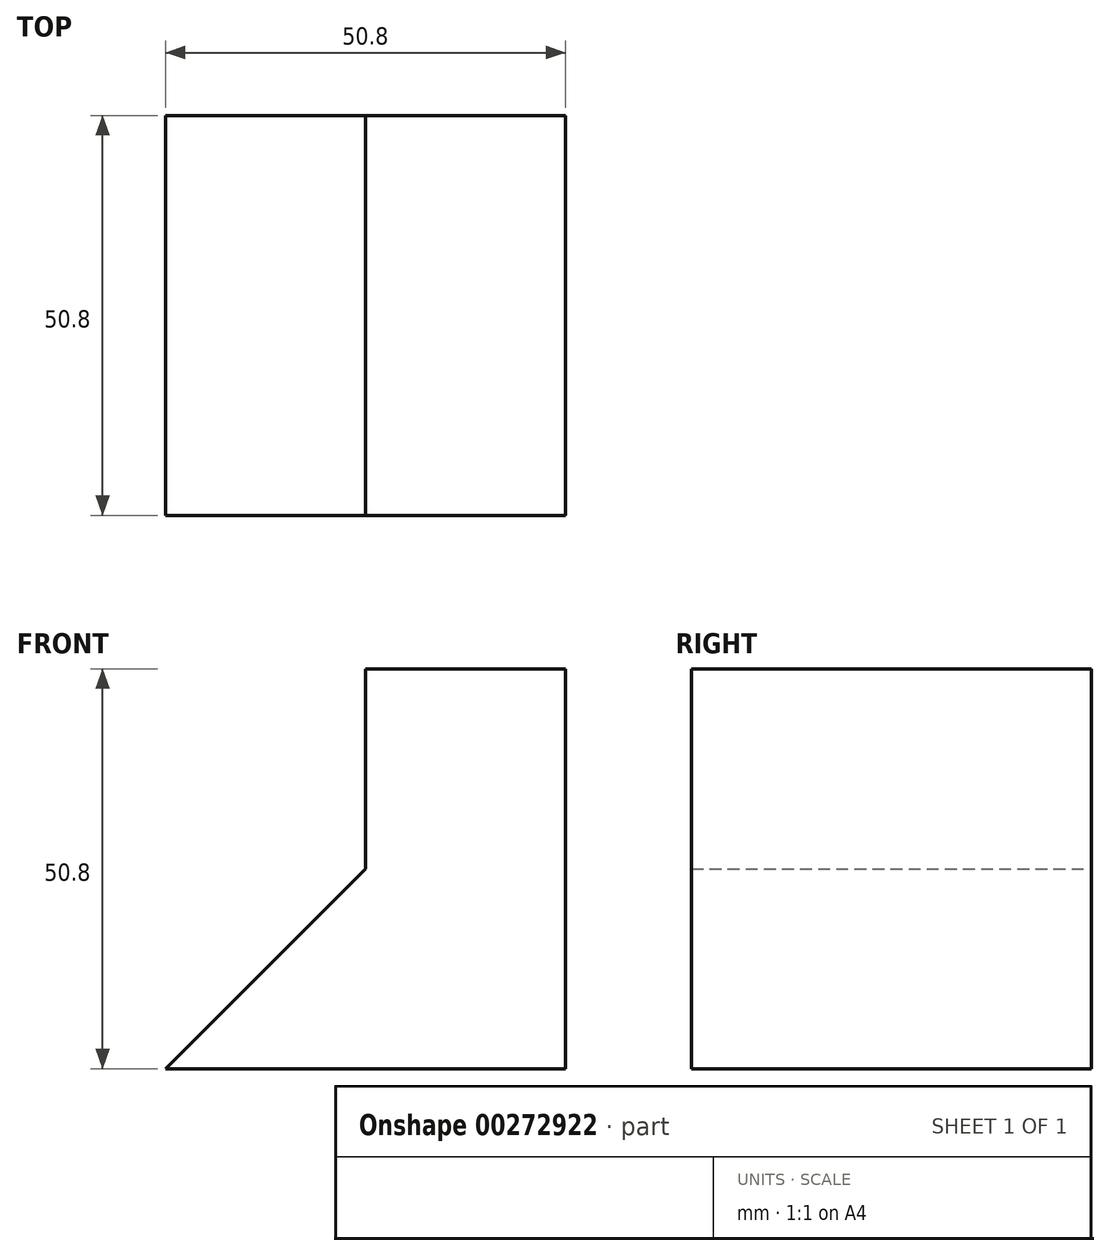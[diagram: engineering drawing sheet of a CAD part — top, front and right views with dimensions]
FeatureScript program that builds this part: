
annotation { "Feature Type Name" : "Feature", "Feature Type Description" : "" }
export const myFeature = defineFeature(function(context is Context, id is Id, definition is map)
    precondition{}
    {
        {
            var Q0;
            Q0=qCreatedBy(makeId("Front.planeOp"),FACE);
            var sketch = newSketch(context, id + "F0", { "sketchPlane" : qUnion([Q0])});
            skLineSegment(sketch, "E0", {"start": v(0, 0) * mm, "end": v(0, 50.8) * mm});
            skLineSegment(sketch, "E1", {"start": v(0, 0) * mm, "end": v(-50.8, 0) * mm});
            skLineSegment(sketch, "E2", {"start": v(0, 50.8) * mm, "end": v(-25.4, 50.8) * mm});
            skLineSegment(sketch, "E3", {"start": v(-25.4, 50.8) * mm, "end": v(-25.4, 25.4) * mm});
            skLineSegment(sketch, "E4", {"start": v(-25.4, 25.4) * mm, "end": v(-50.8, 0) * mm});
            skSolve(sketch);
        }
        {
            var Q0;
            Q0=makeQuery(id+"F0.imprint","IMPRINT",FACE,{"disambiguationData":[TD([[makeQuery(id+"F0.imprint","IMPRINT",EDGE,{"derivedFrom":sQuery(id+"F0.wireOp",EDGE,"E0")}),1.0]])]});
            extrude(context, id + "F1", {"entities" : qUnion([Q0]), "depth" : 50.8 * mm});
        }
    });
